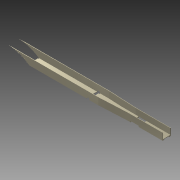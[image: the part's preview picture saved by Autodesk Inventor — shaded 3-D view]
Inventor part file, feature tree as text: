
AUTODESK INVENTOR PART (.ipt)
format: ipt  version: 2015 (Build 190159000, 159)  size: 228,352 bytes
history: native  units: mm
features: extrude x8, sketch x8, shell x1, pattern_linear x1, fillet x1
ambient origin geometry x8: Origin, YZ Plane, XZ Plane, XY Plane, X Axis, Y Axis, Z Axis, Center Point
bodies: 实体1 (feature_tree)
feature tree (19):
  extrude  "拉伸1"  Depth=80.0mm
  extrude  "拉伸2"  Depth=20.0mm
  extrude  "拉伸4"  TaperAngle=135.0deg  [1 undecoded]
  shell  "抽壳2"  Thickness=950.0mm
  extrude  "拉伸5"  Depth=10.0mm
  pattern_linear  "矩形阵列2"  Count1=25  [1 undecoded]
  extrude  "拉伸6"  Depth=200.0mm
  extrude  "拉伸7"  Depth=50.0mm TaperAngle=0.0deg
  extrude  "拉伸8"  Depth=3.0mm
  extrude  "拉伸9"  Depth=40.0mm
  fillet  "圆角2"  Radius=50.0mm
  sketch  "草图1"  dims[d0=950.0mm d1=80.0mm]
  sketch  "草图2"  dims[d2=50.0mm d3=0.0mm d4=20.0mm]
  sketch  "草图4"  dims[d5=5.0mm d6=135.0deg d7=950.0mm d8=0.0mm]
  sketch  "草图5"  dims[d18=10.0mm d19=10.0mm d20=250.0mm]
  sketch  "草图6"  dims[d21=250.0mm d22=200.0mm]
  sketch  "草图7"  dims[d23=200.0mm d24=50.0mm d25=0.0mm]
  sketch  "草图8"  dims[d26=3.0mm d27=5.0mm]
  sketch  "草图10"  dims[d28=25.0mm d29=40.0mm d30=50.0mm d31=0.0mm d32=100.0mm d34=100.0mm d35=22.0mm d36=2.5mm d37=525.0mm d38=80.0mm d39=0.0mm d40=56.0mm d41=172.0mm d42=8.0mm d43=8.0mm d44=80.0mm d45=0.0mm d53=150.0mm d54=0.0mm d55=150.0mm d56=0.0mm d58=3.0mm]
note: 2 required parameter values undecoded (feature->parameter linkage not recoverable at this tier; creation-order binding heuristic only, values carry confidence <= 0.55)
